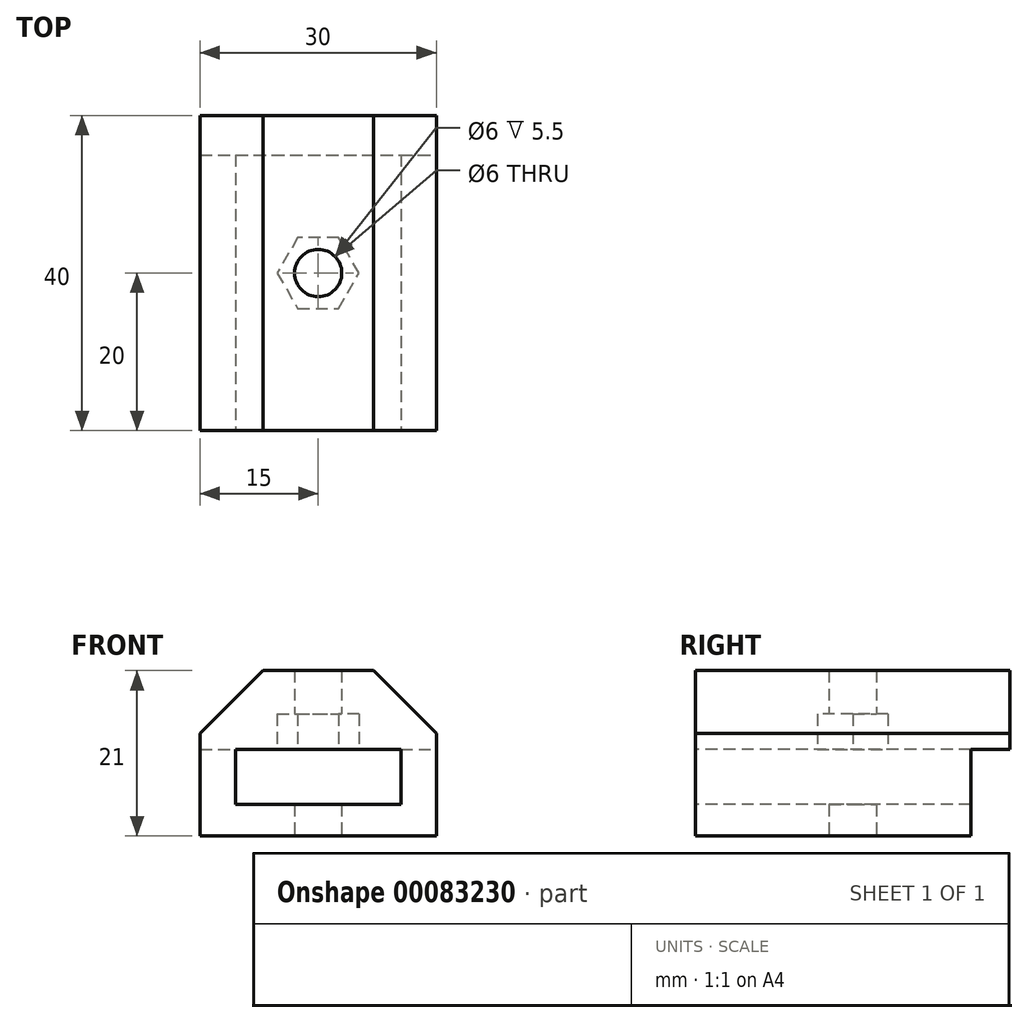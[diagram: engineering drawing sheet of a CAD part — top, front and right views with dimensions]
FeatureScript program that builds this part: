
annotation { "Feature Type Name" : "Feature", "Feature Type Description" : "" }
export const myFeature = defineFeature(function(context is Context, id is Id, definition is map)
    precondition{}
    {
        {
            var Q0;
            Q0=qCreatedBy(makeId("Top.planeOp"),FACE);
            var sketch = newSketch(context, id + "F0", { "sketchPlane" : qUnion([Q0])});
            skLineSegment(sketch, "E0", {"start": v(-47.5, 0) * mm, "end": v(47.5, 0) * mm});
            skLineSegment(sketch, "E1.0", {"start": v(-47.5, 5) * mm, "end": v(47.5, 5) * mm, "construction": true});
            skPoint(sketch, "E2", {"position": v(-40, 5) * mm});
            skPoint(sketch, "E3", {"position": v(40, 5) * mm});
            skLineSegment(sketch, "E4.bottom", {"start": v(-15, 0) * mm, "end": v(15, 0) * mm});
            skLineSegment(sketch, "E4.top", {"start": v(-15, -40) * mm, "end": v(15, -40) * mm});
            skLineSegment(sketch, "E4.left", {"start": v(-15, 0) * mm, "end": v(-15, -40) * mm});
            skLineSegment(sketch, "E4.right", {"start": v(15, 0) * mm, "end": v(15, -40) * mm});
            skLineSegment(sketch, "E5.0", {"start": v(-47.5, -5) * mm, "end": v(47.5, -5) * mm});
            skLineSegment(sketch, "E6", {"start": v(-47.5, -5) * mm, "end": v(-47.5, 0) * mm});
            skLineSegment(sketch, "E7", {"start": v(47.5, -5) * mm, "end": v(47.5, 0) * mm});
            skSolve(sketch);
        }
        {
            var Q0;
            {var subQ0=sQuery(id+"F0.wireOp",EDGE,"E4.top");Q0=makeQuery(id+"F0.imprint","IMPRINT",FACE,{"disambiguationData":[TD([[makeQuery(id+"F0.imprint","IMPRINT",EDGE,{"derivedFrom":subQ0}),1.0]])]});}
            var Q1;
            {var subQ0=sQuery(id+"F0.wireOp",EDGE,"E4.bottom");Q1=makeQuery(id+"F0.imprint","IMPRINT",FACE,{"disambiguationData":[TD([[makeQuery(id+"F0.imprint","IMPRINT",EDGE,{"derivedFrom":subQ0}),-1.0]])]});}
            var Q2;
            Q2=makeQuery(id+"F0.imprint","IMPRINT",FACE,{"disambiguationData":[TD([[makeQuery(id+"F0.imprint","IMPRINT",EDGE,{"derivedFrom":sQuery(id+"F0.wireOp",EDGE,"ns4altNp-ss2W-dFMv-bWeC-xpGnxNBgIdfz")}),-1.0]])]});
            extrude(context, id + "F1", {"entities" : qUnion([Q0, Q1, Q2]), "depth" : 4 * mm});
        }
        {
            var Q0;
            {var subQ0=sQuery(id+"F0.wireOp",EDGE,"E6");var subQ1=sQuery(id+"F0.wireOp",EDGE,"E5.0");var subQ2=sQuery(id+"F0.wireOp",EDGE,"E4.left");var subQ3=sQuery(id+"F0.wireOp",EDGE,"E4.right");var subQ4=sQuery(id+"F0.wireOp",EDGE,"E4.top");var subQ5=sQuery(id+"F0.wireOp",EDGE,"E7");Q0=makeQuery(id+"FZvf6YzPrYx5U73_1.boolean.opBoolean","SPLIT",FACE,{"disambiguationData":[TD([makeQuery(id+"F1.opExtrude","SWEPT_FACE",FACE,{"disambiguationData":[OSD([subQ4])]})])],"derivedFrom":makeQuery(id+"F1.opExtrude","CAP_FACE",FACE,{"disambiguationData":[OSD([sQuery(id+"F0.wireOp",EDGE,"ns4altNp-ss2W-dFMv-bWeC-xpGnxNBgIdfz"),sQuery(id+"F0.wireOp",EDGE,"ic2oWXhY-SUcw-90YI-cqj8-ig1FPsMkjyfk"),sQuery(id+"F0.wireOp",EDGE,"qsv0PS59-A5JC-heU3-Ksa6-Nzkd553XjHmy"),sQuery(id+"F0.wireOp",EDGE,"wU679CG7-L023-bfpu-luHE-NNCgExIXVE5m"),subQ4,subQ2,subQ3,subQ1,subQ0,subQ5])],"isStart":false})});}
            var sketch = newSketch(context, id + "F2", { "sketchPlane" : qUnion([Q0])});
            skLineSegment(sketch, "E8.0", {"start": v(-10.5, 0) * mm, "end": v(-10.5, -40) * mm});
            skLineSegment(sketch, "E9.0", {"start": v(10.5, 0) * mm, "end": v(10.5, -40) * mm});
            skSolve(sketch);
        }
        {
            var Q0;
            {var subQ5=sQuery(id+"F0.wireOp",EDGE,"E4.right");var subQ8=makeQuery(id+"F1.opExtrude","CAP_EDGE",EDGE,{"disambiguationData":[OSD([subQ5])],"isStart":false});Q0=makeQuery(id+"F2.imprint","IMPRINT",FACE,{"disambiguationData":[TD([[makeQuery(id+"F2.imprint","IMPRINT",EDGE,{"derivedFrom":subQ8}),-1.0]])]});}
            var Q1;
            {var subQ5=sQuery(id+"F0.wireOp",EDGE,"E4.left");var subQ8=makeQuery(id+"F1.opExtrude","CAP_EDGE",EDGE,{"disambiguationData":[OSD([subQ5])],"isStart":false});Q1=makeQuery(id+"F2.imprint","IMPRINT",FACE,{"disambiguationData":[TD([[makeQuery(id+"F2.imprint","IMPRINT",EDGE,{"derivedFrom":subQ8}),1.0]])]});}
            extrude(context, id + "F3", {"entities" : qUnion([Q0, Q1]), "operationType" : NewBodyOperationType.ADD, "depth" : 7 * mm});
        }
        {
            var Q0;
            Q0=makeQuery(id+"F3.opExtrude","CAP_FACE",FACE,{"disambiguationData":[OSD([sQuery(id+"F0.wireOp",EDGE,"E4.bottom"),sQuery(id+"F0.wireOp",EDGE,"E4.top"),sQuery(id+"F0.wireOp",EDGE,"E4.right"),sQuery(id+"F2.wireOp",EDGE,"E9.0")])],"isStart":false});
            var sketch = newSketch(context, id + "F4", { "sketchPlane" : qUnion([Q0])});
            skLineSegment(sketch, "E10.bottom", {"start": v(-15, -40) * mm, "end": v(-15, -40) * mm});
            skLineSegment(sketch, "E10.top", {"start": v(-15, -40) * mm, "end": v(-15, -40) * mm});
            skLineSegment(sketch, "E10.left", {"start": v(-15, -40) * mm, "end": v(-15, -40) * mm});
            skLineSegment(sketch, "E10.right", {"start": v(-15, -40) * mm, "end": v(-15, -40) * mm});
            skLineSegment(sketch, "E11.bottom", {"start": v(15, 0) * mm, "end": v(-15, 0) * mm});
            skLineSegment(sketch, "E11.top", {"start": v(15, -40) * mm, "end": v(-15, -40) * mm});
            skLineSegment(sketch, "E11.left", {"start": v(15, 0) * mm, "end": v(15, -40) * mm});
            skLineSegment(sketch, "E11.right", {"start": v(-15, 0) * mm, "end": v(-15, -40) * mm});
            skSolve(sketch);
        }
        {
            var Q0;
            {var subQ0=sQuery(id+"F4.wireOp",EDGE,"E11.left");Q0=makeQuery(id+"F4.imprint","IMPRINT",FACE,{"disambiguationData":[TD([[makeQuery(id+"F4.imprint","IMPRINT",EDGE,{"derivedFrom":subQ0}),-1.0]])]});}
            var Q1;
            {var subQ2=sQuery(id+"F4.wireOp",EDGE,"E11.right");Q1=makeQuery(id+"F4.imprint","IMPRINT",FACE,{"disambiguationData":[TD([[makeQuery(id+"F4.imprint","IMPRINT",EDGE,{"derivedFrom":subQ2}),1.0]])]});}
            extrude(context, id + "F5", {"entities" : qUnion([Q0, Q1]), "operationType" : NewBodyOperationType.ADD, "depth" : 10 * mm});
        }
        {
            var Q0;
            Q0=makeQuery(id+"F5.opExtrude","CAP_FACE",FACE,{"disambiguationData":[OSD([sQuery(id+"F4.wireOp",EDGE,"E11.bottom"),sQuery(id+"F4.wireOp",EDGE,"E11.top"),sQuery(id+"F4.wireOp",EDGE,"E11.left"),sQuery(id+"F4.wireOp",EDGE,"E11.right")])],"isStart":false});
            var sketch = newSketch(context, id + "F6", { "sketchPlane" : qUnion([Q0])});
            skLineSegment(sketch, "E12", {"start": v(-15, 0) * mm, "end": v(15, -40) * mm, "construction": true});
            skPoint(sketch, "E13", {"position": v(0, -20) * mm});
            skSolve(sketch);
        }
        {
            var Q0;
            Q0=sQuery(id+"F6.wireOp",VERTEX,"E13");
            var Q1;
            Q1=makeQuery(id+"F1.opExtrude","SWEPT_BODY",BODY,{"disambiguationData":[OSD([sQuery(id+"F0.wireOp",EDGE,"E4.bottom"),sQuery(id+"F0.wireOp",EDGE,"E4.top"),sQuery(id+"F0.wireOp",EDGE,"E4.left"),sQuery(id+"F0.wireOp",EDGE,"E4.right")])]});
            hole(context, id + "F7", {"style" : HoleStyle.SIMPLE, "endStyle" : HoleEndStyle.THROUGH, "holeDiameter" : 6 * mm, "tappedDepth" : 12 * mm, "tapClearance" : 3, "locations" : qUnion([Q0]), "scope" : qUnion([Q1]), "startStyle" : HoleStartStyle.PART});
        }
        {
            var Q0;
            Q0=makeQuery(id+"F5.opExtrude","CAP_FACE",FACE,{"disambiguationData":[OSD([sQuery(id+"F4.wireOp",EDGE,"E11.bottom"),sQuery(id+"F4.wireOp",EDGE,"E11.top"),sQuery(id+"F4.wireOp",EDGE,"E11.left"),sQuery(id+"F4.wireOp",EDGE,"E11.right")])],"isStart":true});
            var sketch = newSketch(context, id + "F8", { "sketchPlane" : qUnion([Q0])});
            skCircle(sketch, "E14.cCircle", {"center": v(0, 20) * mm, "radius": 4.5 * mm, "construction": true});
            skLineSegment(sketch, "E14.0", {"start": v(-2.6, 24.5) * mm, "end": v(2.6, 24.5) * mm});
            skLineSegment(sketch, "E14.1", {"start": v(2.6, 24.5) * mm, "end": v(5.2, 20) * mm});
            skLineSegment(sketch, "E14.2", {"start": v(5.2, 20) * mm, "end": v(2.6, 15.5) * mm});
            skLineSegment(sketch, "E14.3", {"start": v(2.6, 15.5) * mm, "end": v(-2.6, 15.5) * mm});
            skLineSegment(sketch, "E14.4", {"start": v(-2.6, 15.5) * mm, "end": v(-5.2, 20) * mm});
            skLineSegment(sketch, "E14.5", {"start": v(-5.2, 20) * mm, "end": v(-2.6, 24.5) * mm});
            skPoint(sketch, "E14.0.midPoint", {"position": v(0, 24.5) * mm});
            skSolve(sketch);
        }
        {
            var Q0;
            Q0=makeQuery(id+"F8.imprint","IMPRINT",FACE,{"disambiguationData":[TD([[makeQuery(id+"F8.imprint","IMPRINT",EDGE,{"derivedFrom":sQuery(id+"F8.wireOp",EDGE,"E14.0")}),-1.0]])]});
            extrude(context, id + "F9", {"entities" : qUnion([Q0]), "operationType" : NewBodyOperationType.REMOVE, "oppositeDirection" : true, "depth" : 4.5 * mm});
        }
        {
            var Q0;
            Q0=makeQuery(id+"F5.opExtrude","CAP_EDGE",EDGE,{"disambiguationData":[OSD([sQuery(id+"F4.wireOp",EDGE,"E11.right")])],"isStart":false});
            var Q1;
            Q1=makeQuery(id+"F5.opExtrude","CAP_EDGE",EDGE,{"disambiguationData":[OSD([sQuery(id+"F4.wireOp",EDGE,"E11.left")])],"isStart":false});
            chamfer(context, id + "F10", {"entities" : qUnion([Q0, Q1]), "width" : 8 * mm, "tangentPropagation" : true});
        }
    });
